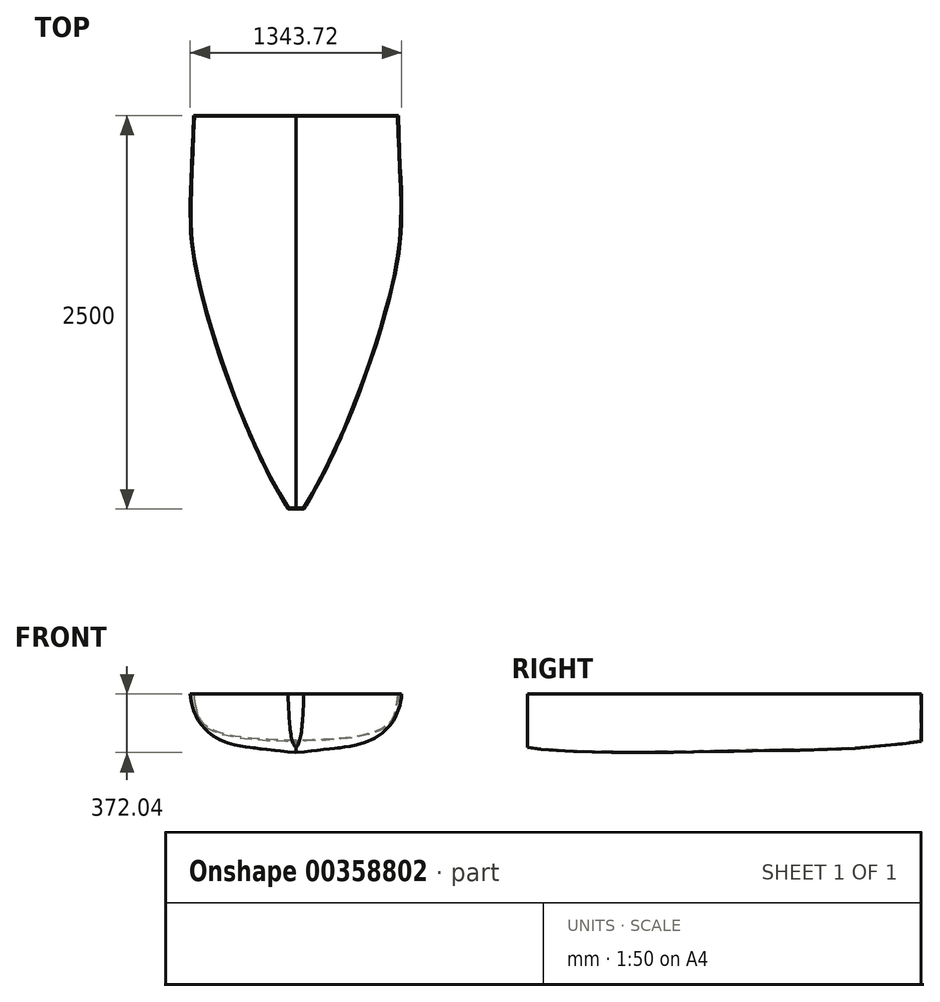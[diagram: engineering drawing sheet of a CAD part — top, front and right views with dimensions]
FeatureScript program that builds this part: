
annotation { "Feature Type Name" : "Feature", "Feature Type Description" : "" }
export const myFeature = defineFeature(function(context is Context, id is Id, definition is map)
    precondition{}
    {
        {
            var Q0;
            Q0=qCreatedBy(makeId("Front.planeOp"),FACE);
            cPlane(context, id + "F0", {"entities" : qUnion([Q0]), "cplaneType" : CPlaneType.OFFSET, "offset" : 1000 * mm, "width" : 150 * mm, "height" : 150 * mm});
        }
        {
            var Q0;
            Q0=qCreatedBy(makeId("Front.planeOp"),FACE);
            var sketch = newSketch(context, id + "F1", { "sketchPlane" : qUnion([Q0])});
            skFitSpline(sketch, "E0", {"points": [v(-650, 0) * mm, v(-541.1, -228.02) * mm, v(0, -300) * mm], "startDerivative": vector(109.64, -1210.35) * mm, "endDerivative": vector(1634.2, -29.3) * mm});
            skFitSpline(sketch, "E1.MirrorCS", {"points": [v(650, 0) * mm, v(541.1, -228.02) * mm, v(0, -300) * mm], "startDerivative": vector(-109.64, -1210.35) * mm, "endDerivative": vector(-1634.2, -29.3) * mm});
            skLineSegment(sketch, "E2", {"start": v(-650, 0) * mm, "end": v(650, 0) * mm});
            skSolve(sketch);
        }
        {
            var Q0;
            Q0=qCreatedBy(id+"F0.planeOp",FACE);
            var sketch = newSketch(context, id + "F2", { "sketchPlane" : qUnion([Q0])});
            skFitSpline(sketch, "E3", {"points": [v(-632, 0) * mm, v(-508.74, -250.24) * mm, v(0, -360) * mm], "startDerivative": vector(12.73, -383.24) * mm, "endDerivative": vector(1316.54, -66.98) * mm});
            skFitSpline(sketch, "E4.MirrorCS", {"points": [v(632, 0) * mm, v(508.74, -250.24) * mm, v(0, -360) * mm], "startDerivative": vector(-12.73, -383.24) * mm, "endDerivative": vector(-1316.54, -66.98) * mm});
            skLineSegment(sketch, "E5", {"start": v(-632, 0) * mm, "end": v(632, 0) * mm});
            skSolve(sketch);
        }
        {
            var Q0;
            Q0=qCreatedBy(makeId("Top.planeOp"),FACE);
            var sketch = newSketch(context, id + "F3", { "sketchPlane" : qUnion([Q0])});
            skFitSpline(sketch, "E6", {"points": [v(-650, 0) * mm, v(-632, -1000) * mm, v(-50, -2500) * mm], "startDerivative": vector(-112.28, -3666.7) * mm, "endDerivative": vector(1403.77, -2222.62) * mm});
            skFitSpline(sketch, "E7.MirrorCS", {"points": [v(650, 0) * mm, v(632, -1000) * mm, v(50, -2500) * mm], "startDerivative": vector(112.28, -3666.7) * mm, "endDerivative": vector(-1403.77, -2222.62) * mm});
            skSolve(sketch);
        }
        {
            var Q0;
            Q0=qCreatedBy(makeId("Right.planeOp"),FACE);
            var sketch = newSketch(context, id + "F4", { "sketchPlane" : qUnion([Q0])});
            skFitSpline(sketch, "E8", {"points": [v(-2500, -340) * mm, v(-1000, -360) * mm, v(0, -300) * mm], "startDerivative": vector(1804.2, -281.69) * mm, "endDerivative": vector(2888.18, 402.34) * mm});
            skSolve(sketch);
        }
        {
            var Q0;
            Q0=qCreatedBy(makeId("Front.planeOp"),FACE);
            cPlane(context, id + "F5", {"entities" : qUnion([Q0]), "cplaneType" : CPlaneType.OFFSET, "offset" : 2500 * mm, "width" : 150 * mm, "height" : 150 * mm});
        }
        {
            var Q0;
            Q0=qCreatedBy(id+"F5.planeOp",FACE);
            var sketch = newSketch(context, id + "F6", { "sketchPlane" : qUnion([Q0])});
            skFitSpline(sketch, "E9", {"points": [v(-50, 0) * mm, v(0, -340) * mm], "startDerivative": vector(15.71, -443.95) * mm, "endDerivative": vector(116.25, -69.36) * mm});
            skFitSpline(sketch, "E10.MirrorCS", {"points": [v(50, 0) * mm, v(0, -340) * mm], "startDerivative": vector(-15.71, -443.95) * mm, "endDerivative": vector(-116.25, -69.36) * mm});
            skLineSegment(sketch, "E11", {"start": v(-50, 0) * mm, "end": v(50, 0) * mm});
            skSolve(sketch);
        }
        {
            var Q0;
            Q0=makeQuery(id+"F1.imprint","IMPRINT",FACE,{"disambiguationData":[TD([[makeQuery(id+"F1.imprint","IMPRINT",EDGE,{"derivedFrom":sQuery(id+"F1.wireOp",EDGE,"E0")}),1.0]])]});
            var Q1;
            Q1=makeQuery(id+"F2.imprint","IMPRINT",FACE,{"disambiguationData":[TD([[makeQuery(id+"F2.imprint","IMPRINT",EDGE,{"derivedFrom":sQuery(id+"F2.wireOp",EDGE,"E3")}),1.0]])]});
            var Q2;
            Q2=makeQuery(id+"F6.imprint","IMPRINT",FACE,{"disambiguationData":[TD([[makeQuery(id+"F6.imprint","IMPRINT",EDGE,{"derivedFrom":sQuery(id+"F6.wireOp",EDGE,"E9")}),1.0]])]});
            var Q3;
            Q3=sQuery(id+"F3.wireOp",EDGE,"E6");
            var Q4;
            Q4=sQuery(id+"F3.wireOp",EDGE,"E7.MirrorCS");
            var Q5;
            Q5=sQuery(id+"F4.wireOp",EDGE,"E8");
            loft(context, id + "F7", {"addGuides" : true, "sheetProfilesArray" : [{ "sheetProfileEntities" : qUnion([Q0]) }, { "sheetProfileEntities" : qUnion([Q1]) }, { "sheetProfileEntities" : qUnion([Q2]) }], "guidesArray" : [{ "guideEntities" : qUnion([Q3]), "guideDerivativeType" : LoftGuideDerivativeType.DEFAULT, "guideDerivativeMagnitude" : 1 }, { "guideEntities" : qUnion([Q4]), "guideDerivativeType" : LoftGuideDerivativeType.DEFAULT, "guideDerivativeMagnitude" : 1 }, { "guideEntities" : qUnion([Q5]), "guideDerivativeType" : LoftGuideDerivativeType.DEFAULT, "guideDerivativeMagnitude" : 1 }]});
        }
        {
            var Q0;
            Q0=makeQuery(id+"F7.opLoft","SWEPT_FACE",FACE,{"disambiguationData":[OSD([sQuery(id+"F1.wireOp",EDGE,"E0"),sQuery(id+"F1.wireOp",EDGE,"E2"),sQuery(id+"F2.wireOp",EDGE,"E5"),sQuery(id+"F3.wireOp",EDGE,"E6"),sQuery(id+"F3.wireOp",EDGE,"E7.MirrorCS")])]});
            shell(context, id + "F8", {"entities" : qUnion([Q0]), "thickness" : 5 * mm});
        }
    });
